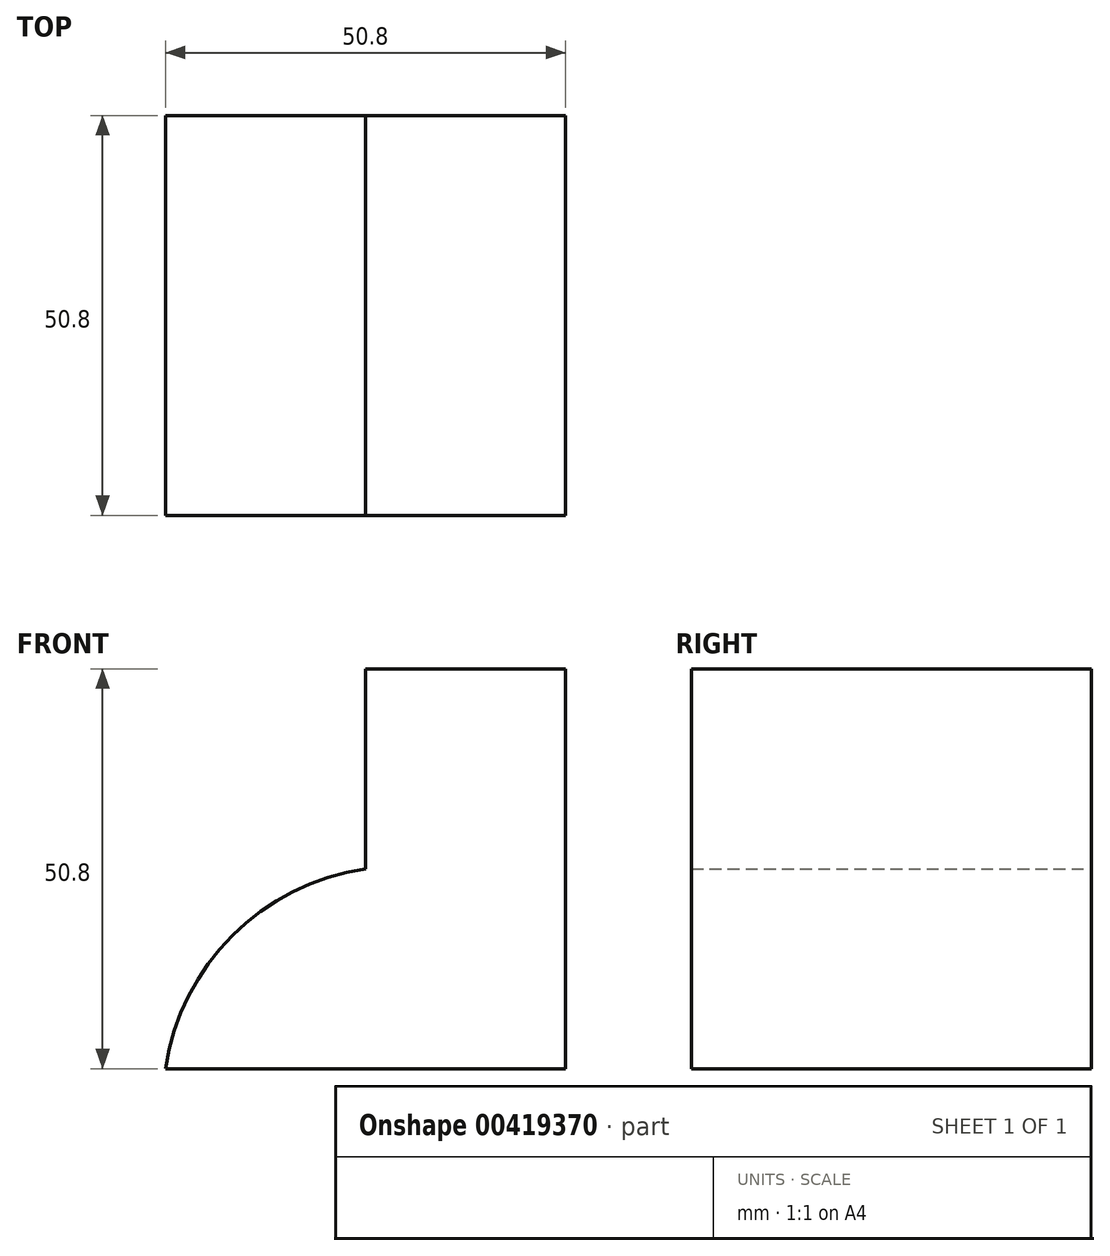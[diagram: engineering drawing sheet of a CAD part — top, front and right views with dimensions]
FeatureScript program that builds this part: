
annotation { "Feature Type Name" : "Feature", "Feature Type Description" : "" }
export const myFeature = defineFeature(function(context is Context, id is Id, definition is map)
    precondition{}
    {
        {
            var Q0;
            Q0=qCreatedBy(makeId("Front.planeOp"),FACE);
            var sketch = newSketch(context, id + "F0", { "sketchPlane" : qUnion([Q0])});
            skLineSegment(sketch, "E0", {"start": v(-29.79, -7.83) * mm, "end": v(-29.79, 17.57) * mm});
            skLineSegment(sketch, "E1", {"start": v(-29.79, 17.57) * mm, "end": v(-4.39, 17.57) * mm});
            skLineSegment(sketch, "E2", {"start": v(-4.39, 17.57) * mm, "end": v(-4.39, -33.23) * mm});
            skLineSegment(sketch, "E3", {"start": v(-4.39, -33.23) * mm, "end": v(-55.19, -33.23) * mm});
            skArc(sketch, "E4", {"start": v(-29.79, -7.83) * mm, "mid": v(-46.7, -16.32) * mm, "end": v(-55.19, -33.23) * mm});
            skSolve(sketch);
        }
        {
            var Q0;
            Q0 = qSketchRegion(id + "F0", true);
            extrude(context, id + "F1", {"entities" : qUnion([Q0]), "depth" : 50.8 * mm});
        }
    });
